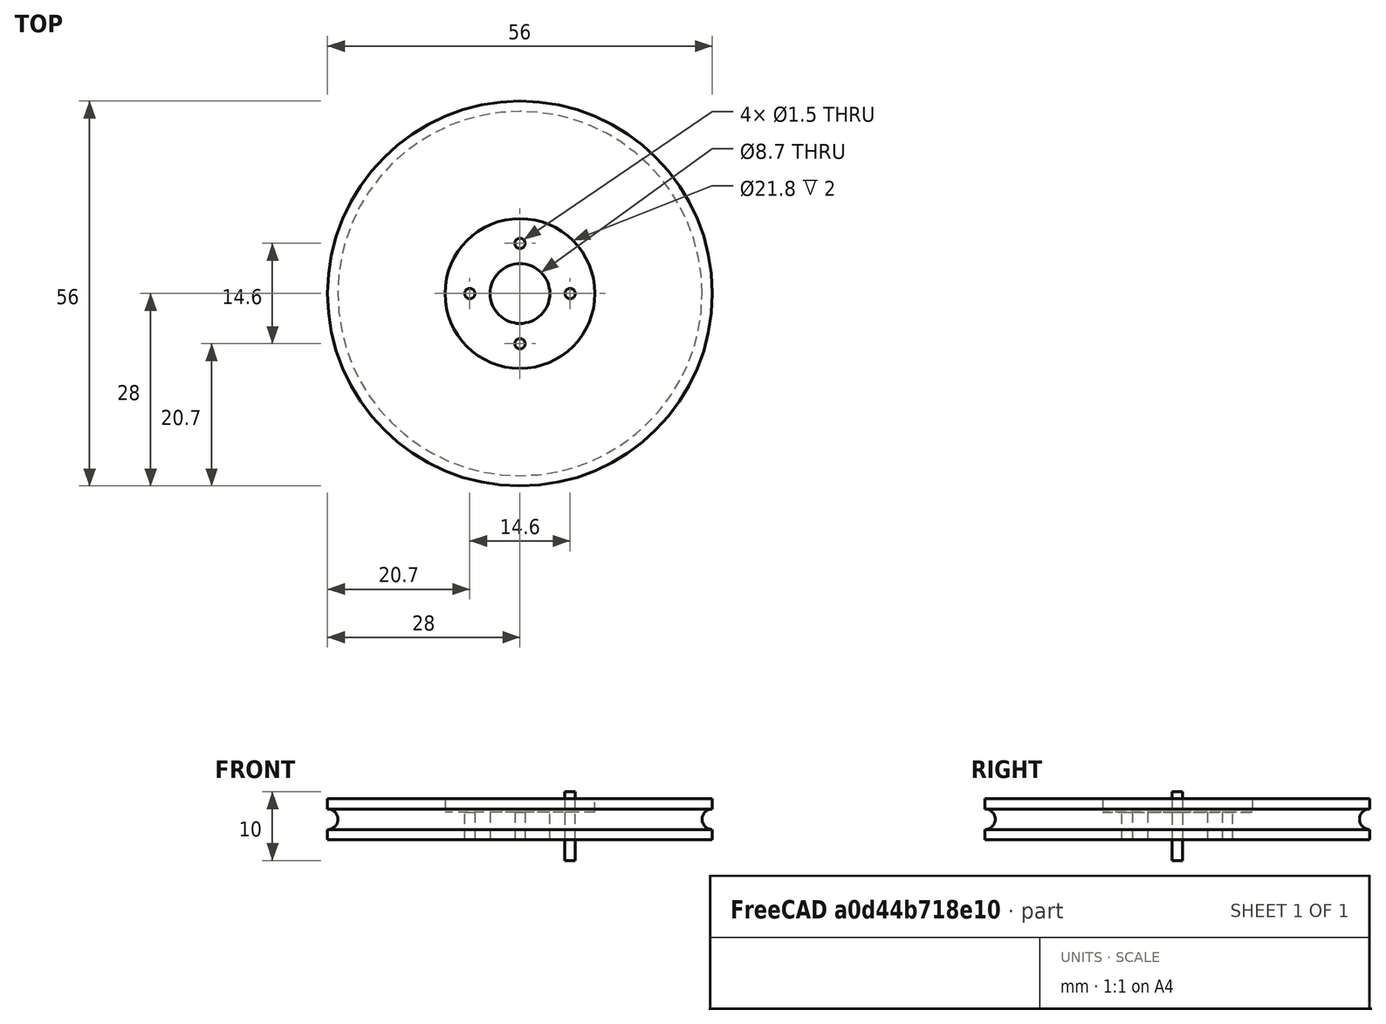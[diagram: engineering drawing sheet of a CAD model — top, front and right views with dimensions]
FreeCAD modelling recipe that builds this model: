
FCSTD DOCUMENT  (FreeCAD 1.0R39319 (Git))
Label: ojt1_t15p01_mini_skybot
License: All rights reserved
LicenseURL: https://en.wikipedia.org/wiki/All_rights_reserved
objects: Part::Cylinder×4, Part::Cut×4, Part::Torus×1, Part::FeaturePython×1
note: 9 computed .brp shape members not serialized (recipe doc carries the construction recipe); baked Part::Feature solids carry a one-line shape summary decoded from their .brp

FEATURE [Part::Cylinder] Cylinder  label="rueda base"
  Angle = 360
  AttacherType = Attacher::AttachEngine3D
  FirstAngle = 0
  Height = 6
  Placement = pos=(0,0,-3) rot=(0,0,1;0rad)
  Radius = 28
  SecondAngle = 0
FEATURE [Part::Torus] Torus  label="hueco-junta-tórica"
  Angle1 = -180
  Angle2 = 180
  Angle3 = 360
  AttacherType = Attacher::AttachEngine3D
  Radius1 = 28
  Radius2 = 1.5
FEATURE [Part::Cut] Cut  label="rueda básica"
  Base = -> Cylinder
  Refine = true
  Tool = -> Torus
FEATURE [Part::Cylinder] Cylinder001  label="corona servo"
  Angle = 360
  AttacherType = Attacher::AttachEngine3D
  FirstAngle = 0
  Height = 10
  Placement = pos=(0,0,1) rot=(0,0,1;0rad)
  Radius = 10.9
  SecondAngle = 0
FEATURE [Part::Cut] Cut001  label="rueda-con-hueco-corona"
  Base = -> Cut
  Refine = true
  Tool = -> Cylinder001
FEATURE [Part::Cylinder] Cylinder002  label="hueco-eje"
  Angle = 360
  AttacherType = Attacher::AttachEngine3D
  FirstAngle = 0
  Height = 10
  Placement = pos=(0,0,-6) rot=(0,0,1;0rad)
  Radius = 4.35
  SecondAngle = 0
FEATURE [Part::Cut] Cut002  label="rueda-corona-eje"
  Base = -> Cut001
  Refine = true
  Tool = -> Cylinder002
FEATURE [Part::Cylinder] Cylinder003  label="taladro"
  Angle = 360
  AttacherType = Attacher::AttachEngine3D
  FirstAngle = 0
  Height = 10
  Placement = pos=(7.3,0,-6) rot=(0,0,1;0rad)
  Radius = 0.75
  SecondAngle = 0
FEATURE [Part::FeaturePython] Array  # Draft array (typed FeaturePython)
  AlwaysSyncPlacement = false
  Angle = 360
  ArrayType = 1
  Axis = (0,0,1)
  Base = -> Cylinder003
  Center = (0,0,0)
  Count = 4
  ExpandArray = false
  Fuse = false
  IntervalAxis = (0,0,0)
  IntervalX = (100,0,0)
  IntervalY = (0,100,0)
  IntervalZ = (0,0,100)
  NumberCircles = 3
  NumberPolar = 4
  NumberX = 2
  NumberY = 2
  NumberZ = 1
  PlacementList = 4 placements: [(7.3,0,-6),(0,7.3,-6),(-7.3,8.93992e-16,-6),(-1.62093e-15,-7.3,-6)]
  RadialDistance = 50
  ScaleList = (4) [(1,1,1),(1,1,1),(1,1,1),(1,1,1)]
  Symmetry = 1
  TangentialDistance = 25
FEATURE [Part::Cut] Cut003  label="rueda miniskybot"
  Base = -> Cut002
  Refine = true
  Tool = -> Array
